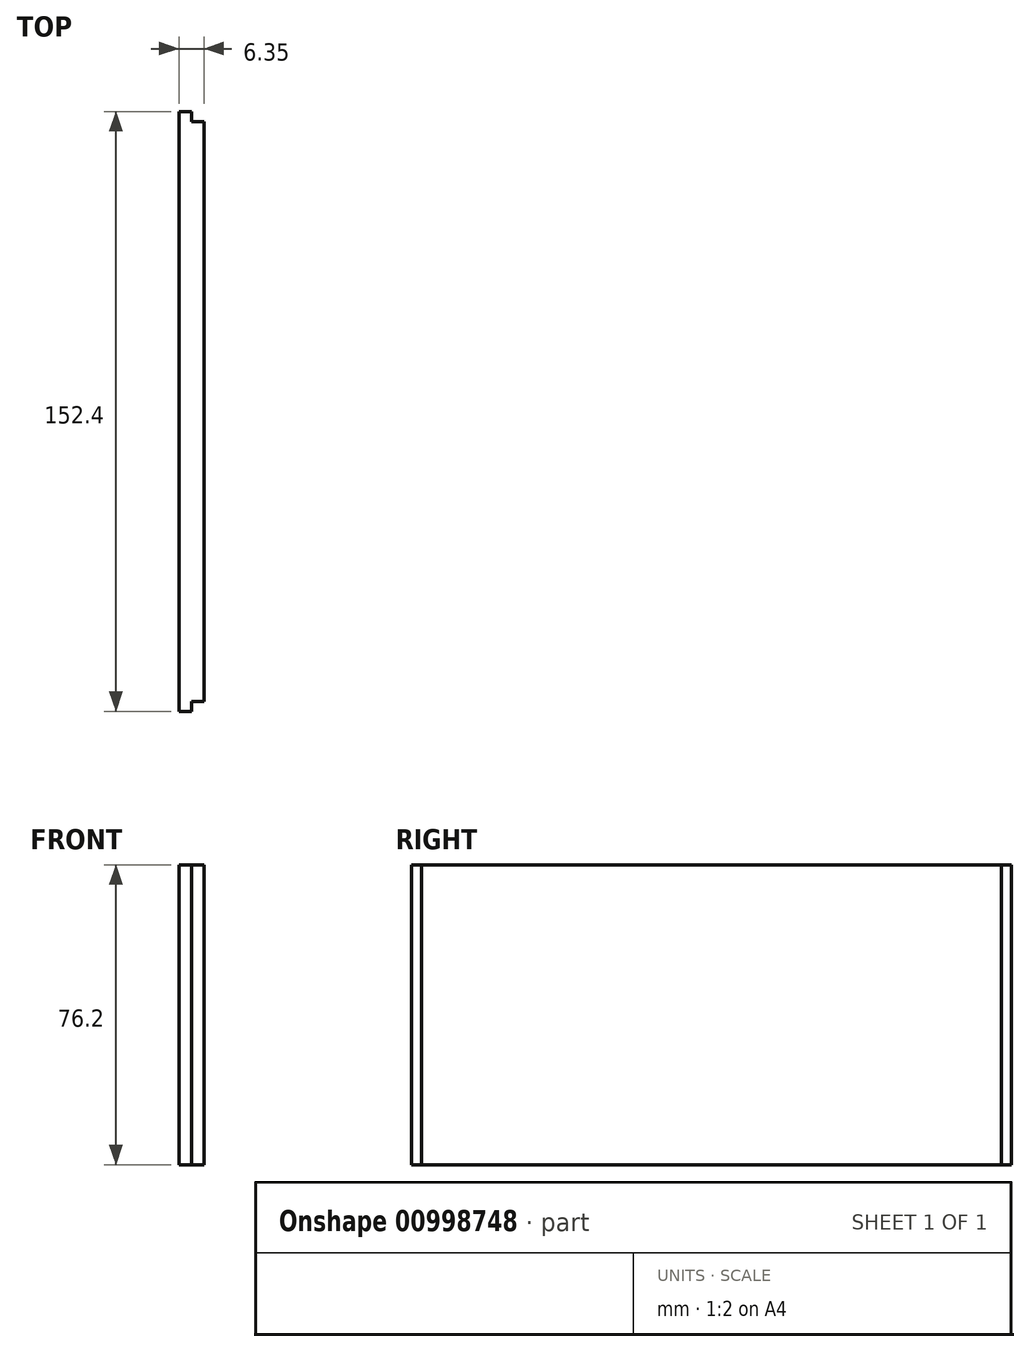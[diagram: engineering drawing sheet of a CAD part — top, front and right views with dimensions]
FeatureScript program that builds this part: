
annotation { "Feature Type Name" : "Feature", "Feature Type Description" : "" }
export const myFeature = defineFeature(function(context is Context, id is Id, definition is map)
    precondition{}
    {
        {
            var Q0;
            Q0=qCreatedBy(makeId("Right.planeOp"),FACE);
            var sketch = newSketch(context, id + "F0", { "sketchPlane" : qUnion([Q0])});
            skLineSegment(sketch, "E0.bottom", {"start": v(-76.2, 38.1) * mm, "end": v(76.2, 38.1) * mm});
            skLineSegment(sketch, "E0.top", {"start": v(-76.2, -38.1) * mm, "end": v(76.2, -38.1) * mm});
            skLineSegment(sketch, "E0.left", {"start": v(-76.2, 38.1) * mm, "end": v(-76.2, -38.1) * mm});
            skLineSegment(sketch, "E0.right", {"start": v(76.2, 38.1) * mm, "end": v(76.2, -38.1) * mm});
            skPoint(sketch, "E0.middle", {"position": v(0, 0) * mm});
            skSolve(sketch);
        }
        {
            var Q0;
            Q0 = qSketchRegion(id + "F0", true);
            extrude(context, id + "F1", {"entities" : qUnion([Q0]), "depth" : 6.35 * mm, "offsetDistance" : 25.4 * mm});
        }
        {
            var Q0;
            Q0=makeQuery(id+"F1.opExtrude","SWEPT_FACE",FACE,{"disambiguationData":[OSD([sQuery(id+"F0.wireOp",EDGE,"E0.top")])]});
            var sketch = newSketch(context, id + "F2", { "sketchPlane" : qUnion([Q0])});
            skLineSegment(sketch, "E1", {"start": v(3.18, 76.2) * mm, "end": v(3.18, 73.66) * mm});
            skLineSegment(sketch, "E2", {"start": v(3.18, 73.66) * mm, "end": v(6.35, 73.66) * mm});
            skLineSegment(sketch, "E3", {"start": v(6.35, 73.66) * mm, "end": v(6.35, 76.2) * mm});
            skLineSegment(sketch, "E4", {"start": v(6.35, 76.2) * mm, "end": v(3.18, 76.2) * mm});
            skSolve(sketch);
        }
        {
            var Q0;
            Q0 = qSketchRegion(id + "F2", true);
            extrude(context, id + "F3", {"entities" : qUnion([Q0]), "operationType" : NewBodyOperationType.REMOVE, "oppositeDirection" : true, "depth" : 152.4 * mm, "offsetDistance" : 25.4 * mm});
        }
        {
            var Q0;
            Q0=makeQuery(id+"F1.opExtrude","SWEPT_FACE",FACE,{"disambiguationData":[OSD([sQuery(id+"F0.wireOp",EDGE,"E0.top")])]});
            var sketch = newSketch(context, id + "F4", { "sketchPlane" : qUnion([Q0])});
            skLineSegment(sketch, "E5", {"start": v(3.18, -76.2) * mm, "end": v(3.18, -73.66) * mm});
            skLineSegment(sketch, "E6", {"start": v(3.18, -73.66) * mm, "end": v(6.35, -73.66) * mm});
            skLineSegment(sketch, "E7", {"start": v(6.35, -76.2) * mm, "end": v(3.18, -76.2) * mm});
            skLineSegment(sketch, "E8", {"start": v(6.35, -73.66) * mm, "end": v(6.35, -76.2) * mm});
            skSolve(sketch);
        }
        {
            var Q0;
            Q0=makeQuery(id+"F4.imprint","IMPRINT",FACE,{"disambiguationData":[TD([[makeQuery(id+"F4.imprint","IMPRINT",EDGE,{"derivedFrom":sQuery(id+"F4.wireOp",EDGE,"E5")}),-1.0]])]});
            extrude(context, id + "F5", {"entities" : qUnion([Q0]), "operationType" : NewBodyOperationType.REMOVE, "oppositeDirection" : true, "depth" : 152.4 * mm, "offsetDistance" : 25.4 * mm});
        }
    });
